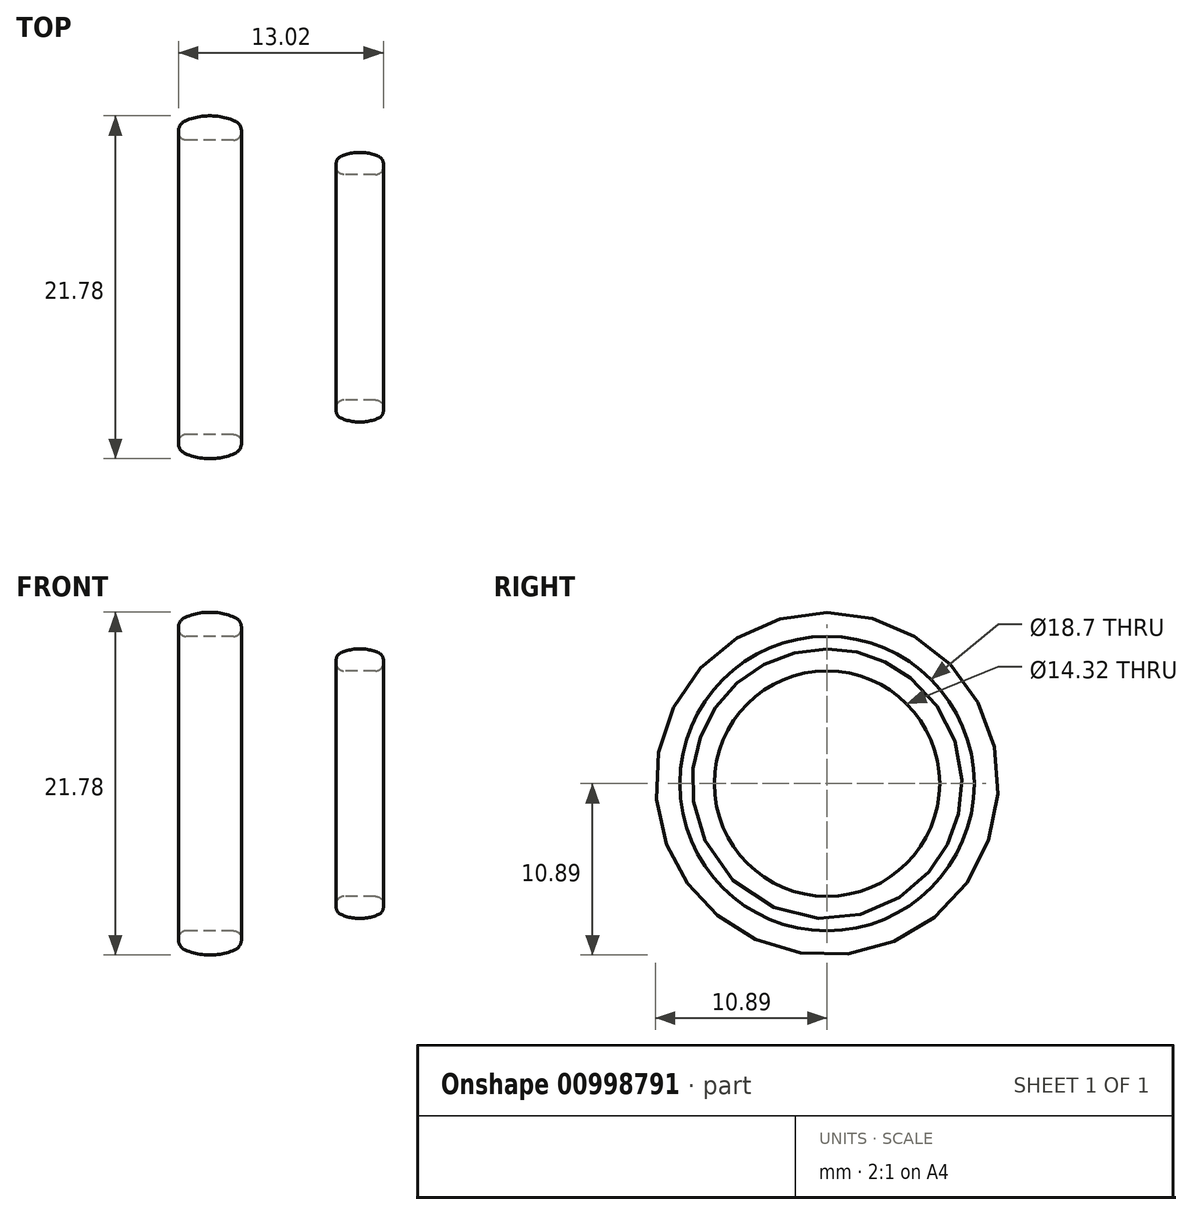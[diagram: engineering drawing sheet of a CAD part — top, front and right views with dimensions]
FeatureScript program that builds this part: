
annotation { "Feature Type Name" : "Feature", "Feature Type Description" : "" }
export const myFeature = defineFeature(function(context is Context, id is Id, definition is map)
    precondition{}
    {
        {
            var Q0;
            Q0=qCreatedBy(makeId("Front.planeOp"),FACE);
            var sketch = newSketch(context, id + "F0", { "sketchPlane" : qUnion([Q0])});
            skLineSegment(sketch, "E0", {"start": v(-1.5, 9.35) * mm, "end": v(1.5, 9.35) * mm});
            skLineSegment(sketch, "E1", {"start": v(-2, 9.85) * mm, "end": v(-2, 9.92) * mm});
            skLineSegment(sketch, "E2", {"start": v(2, 9.85) * mm, "end": v(2, 9.92) * mm});
            skArc(sketch, "E3", {"start": v(1.58, 10.56) * mm, "mid": v(0, 10.89) * mm, "end": v(-1.58, 10.56) * mm});
            skPoint(sketch, "E4.visualSharp", {"position": v(-2, 10.35) * mm});
            skArc(sketch, "E4.filletArc", {"start": v(-1.58, 10.56) * mm, "mid": v(-1.88, 10.3) * mm, "end": v(-2, 9.92) * mm});
            skPoint(sketch, "E5.visualSharp", {"position": v(-2, 9.35) * mm});
            skArc(sketch, "E5.filletArc", {"start": v(-2, 9.85) * mm, "mid": v(-1.85, 9.5) * mm, "end": v(-1.5, 9.35) * mm});
            skPoint(sketch, "E6.visualSharp", {"position": v(2, 9.35) * mm});
            skArc(sketch, "E6.filletArc", {"start": v(1.5, 9.35) * mm, "mid": v(1.85, 9.5) * mm, "end": v(2, 9.85) * mm});
            skPoint(sketch, "E7.visualSharp", {"position": v(2, 10.35) * mm});
            skArc(sketch, "E7.filletArc", {"start": v(2, 9.92) * mm, "mid": v(1.88, 10.3) * mm, "end": v(1.58, 10.56) * mm});
            skLineSegment(sketch, "E8", {"start": v(-11.97, 0) * mm, "end": v(12.2, 0) * mm});
            skLineSegment(sketch, "E9", {"start": v(8.52, 7.16) * mm, "end": v(10.52, 7.16) * mm});
            skLineSegment(sketch, "E10", {"start": v(8.02, 7.66) * mm, "end": v(8.02, 7.85) * mm});
            skLineSegment(sketch, "E11", {"start": v(11.02, 7.66) * mm, "end": v(11.02, 7.85) * mm});
            skArc(sketch, "E12", {"start": v(10.72, 8.31) * mm, "mid": v(9.52, 8.56) * mm, "end": v(8.32, 8.31) * mm});
            skPoint(sketch, "E13.visualSharp", {"position": v(8.02, 8.16) * mm});
            skArc(sketch, "E13.filletArc", {"start": v(8.32, 8.31) * mm, "mid": v(8.1, 8.13) * mm, "end": v(8.02, 7.85) * mm});
            skPoint(sketch, "E14.visualSharp", {"position": v(8.02, 7.16) * mm});
            skArc(sketch, "E14.filletArc", {"start": v(8.02, 7.66) * mm, "mid": v(8.16, 7.3) * mm, "end": v(8.52, 7.16) * mm});
            skPoint(sketch, "E15.visualSharp", {"position": v(11.02, 7.16) * mm});
            skArc(sketch, "E15.filletArc", {"start": v(10.52, 7.16) * mm, "mid": v(10.87, 7.3) * mm, "end": v(11.02, 7.66) * mm});
            skPoint(sketch, "E16.visualSharp", {"position": v(11.02, 8.16) * mm});
            skArc(sketch, "E16.filletArc", {"start": v(11.02, 7.85) * mm, "mid": v(10.93, 8.13) * mm, "end": v(10.72, 8.31) * mm});
            skLineSegment(sketch, "E17", {"start": v(0, 14.34) * mm, "end": v(0, 6.37) * mm});
            skPoint(sketch, "E18", {"position": v(0, 10.89) * mm});
            skSolve(sketch);
        }
        {
            var Q0;
            Q0=makeQuery(id+"F0.imprint","IMPRINT",FACE,{"disambiguationData":[TD([[makeQuery(id+"F0.imprint","IMPRINT",EDGE,{"derivedFrom":sQuery(id+"F0.wireOp",EDGE,"E0")}),1.0]])]});
            var Q1;
            Q1=makeQuery(id+"F0.imprint","IMPRINT",FACE,{"disambiguationData":[TD([[makeQuery(id+"F0.imprint","IMPRINT",EDGE,{"derivedFrom":sQuery(id+"F0.wireOp",EDGE,"E9")}),1.0]])]});
            var Q2;
            Q2=sQuery(id+"F0.wireOp",EDGE,"E8");
            revolve(context, id + "F1", {"surfaceOperationType" : NewSurfaceOperationType.NEW, "entities" : qUnion([Q0, Q1]), "axis" : qUnion([Q2]), "revolveType" : RevolveType.FULL});
        }
    });
